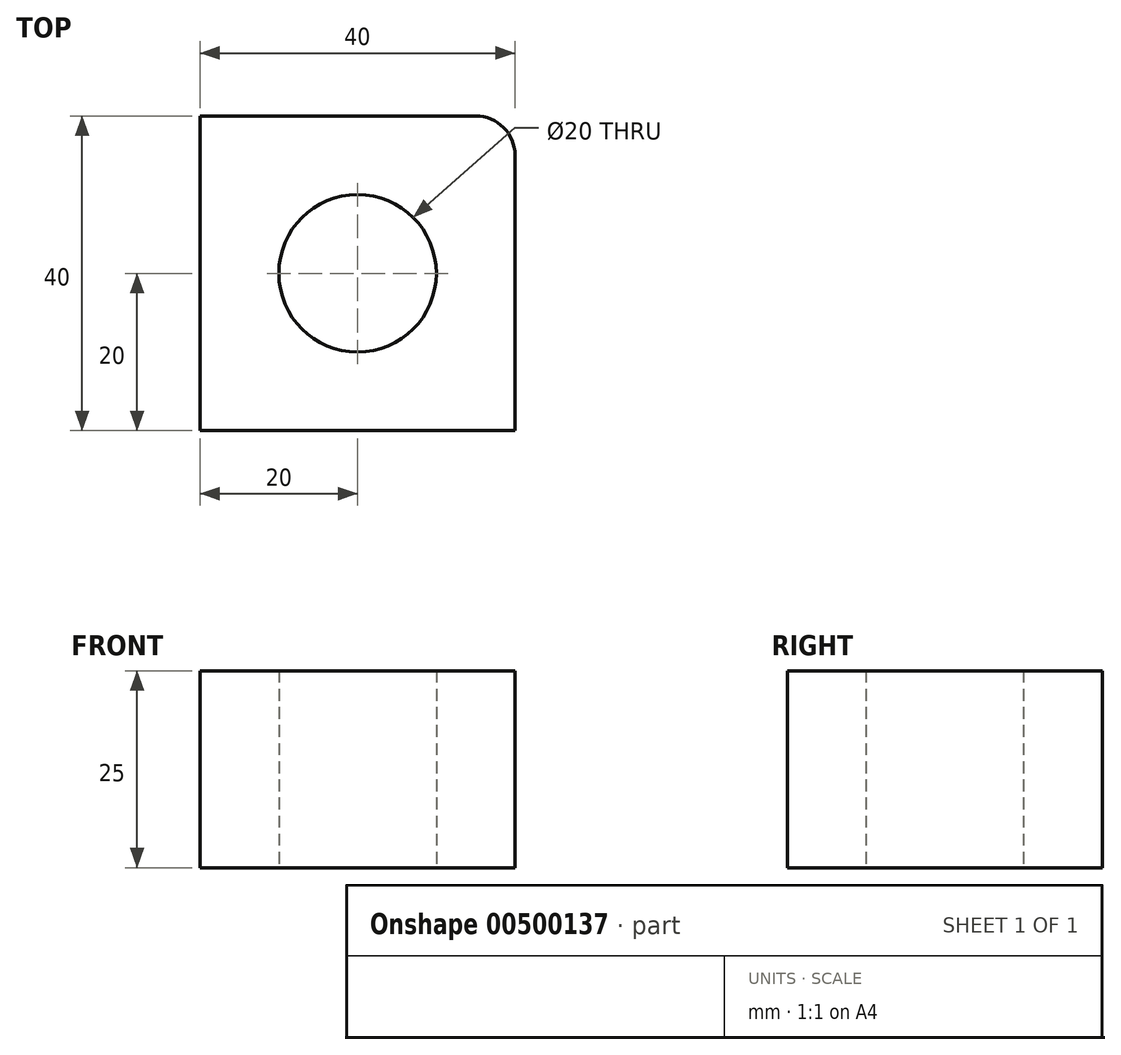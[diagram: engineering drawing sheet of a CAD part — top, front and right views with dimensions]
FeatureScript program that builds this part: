
annotation { "Feature Type Name" : "Feature", "Feature Type Description" : "" }
export const myFeature = defineFeature(function(context is Context, id is Id, definition is map)
    precondition{}
    {
        {
            var Q0;
            Q0=qCreatedBy(makeId("Top.planeOp"),FACE);
            var sketch = newSketch(context, id + "F0", { "sketchPlane" : qUnion([Q0])});
            skLineSegment(sketch, "E0.bottom", {"start": v(0, 0) * mm, "end": v(40, 0) * mm});
            skLineSegment(sketch, "E0.top", {"start": v(0, 40) * mm, "end": v(35, 40) * mm});
            skLineSegment(sketch, "E0.left", {"start": v(0, 0) * mm, "end": v(0, 40) * mm});
            skLineSegment(sketch, "E0.right", {"start": v(40, 0) * mm, "end": v(40, 35) * mm});
            skPoint(sketch, "E1.visualSharp", {"position": v(40, 40) * mm});
            skArc(sketch, "E1.filletArc", {"start": v(40, 35) * mm, "mid": v(38.54, 38.54) * mm, "end": v(35, 40) * mm});
            skPoint(sketch, "E2.centerSnap0", {"position": v(20, 0) * mm});
            skPoint(sketch, "E2.centerSnap1", {"position": v(0, 20) * mm});
            skCircle(sketch, "E3", {"center": v(20, 20) * mm, "radius": 10 * mm});
            skSolve(sketch);
        }
        {
            var Q0;
            Q0=makeQuery(id+"F0.imprint","IMPRINT",FACE,{"disambiguationData":[TD([[makeQuery(id+"F0.imprint","IMPRINT",EDGE,{"derivedFrom":sQuery(id+"F0.wireOp",EDGE,"E0.bottom")}),1.0]])]});
            extrude(context, id + "F1", {"entities" : qUnion([Q0]), "depth" : 25 * mm});
        }
    });
